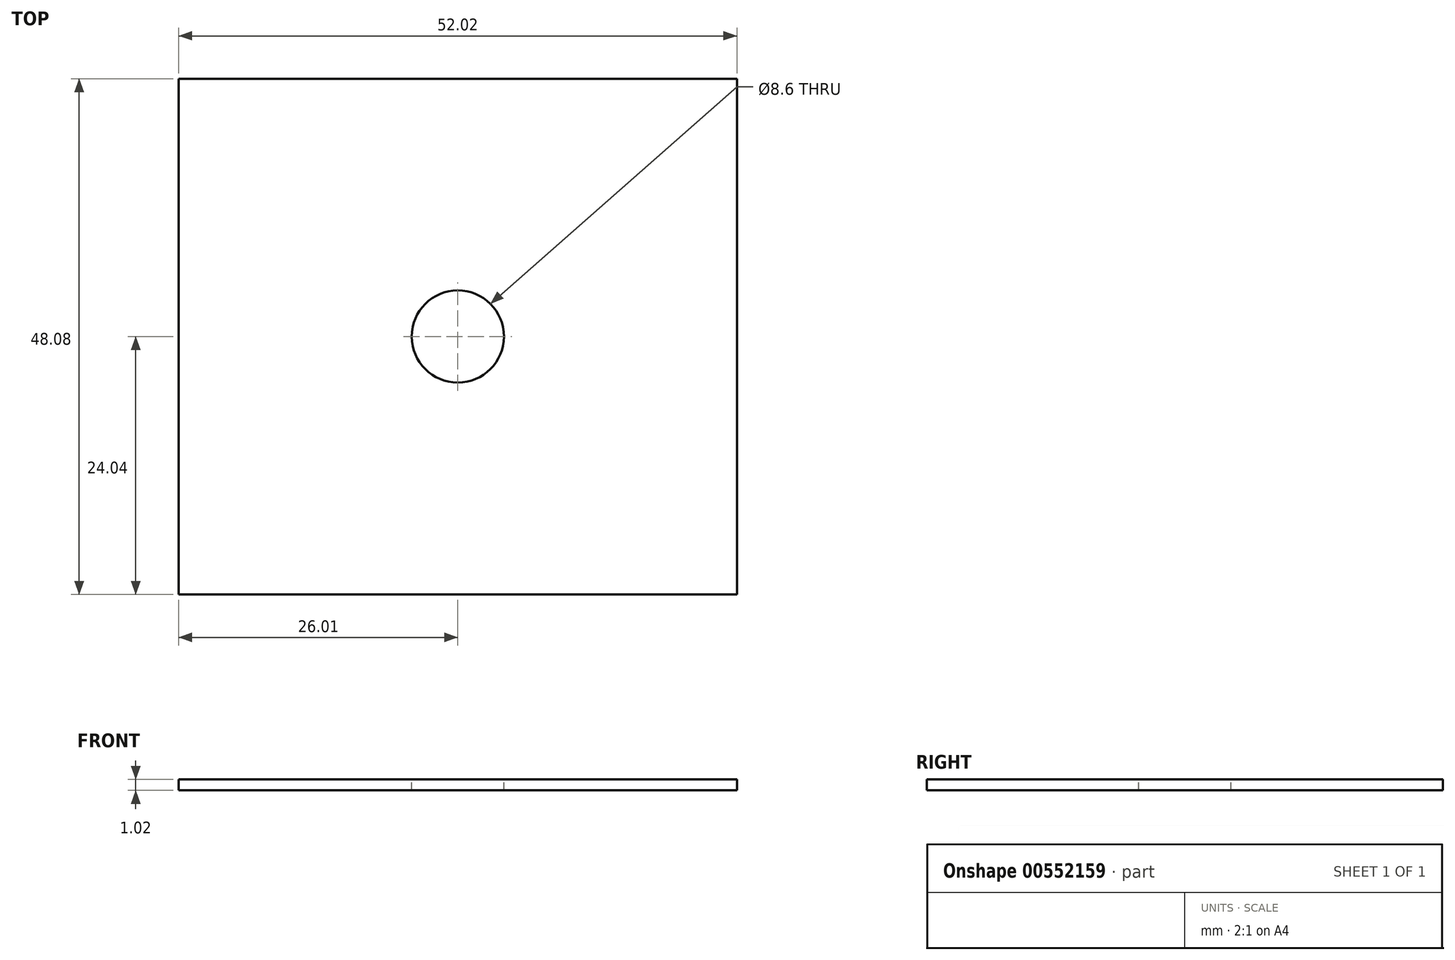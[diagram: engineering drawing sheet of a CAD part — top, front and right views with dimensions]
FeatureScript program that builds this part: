
annotation { "Feature Type Name" : "Feature", "Feature Type Description" : "" }
export const myFeature = defineFeature(function(context is Context, id is Id, definition is map)
    precondition{}
    {
        {
            var Q0;
            Q0=qCreatedBy(makeId("Top.planeOp"),FACE);
            var sketch = newSketch(context, id + "F0", { "sketchPlane" : qUnion([Q0])});
            skLineSegment(sketch, "E0.bottom", {"start": v(26.01, -24.04) * mm, "end": v(-26.01, -24.04) * mm});
            skLineSegment(sketch, "E0.top", {"start": v(26.01, 24.04) * mm, "end": v(-26.01, 24.04) * mm});
            skLineSegment(sketch, "E0.left", {"start": v(26.01, -24.04) * mm, "end": v(26.01, 24.04) * mm});
            skLineSegment(sketch, "E0.right", {"start": v(-26.01, -24.04) * mm, "end": v(-26.01, 24.04) * mm});
            skPoint(sketch, "E0.middle", {"position": v(0, 0) * mm});
            skSolve(sketch);
        }
        {
            var Q0;
            Q0 = qSketchRegion(id + "F0", true);
            extrude(context, id + "F1", {"entities" : qUnion([Q0]), "depth" : 1.02 * mm, "offsetDistance" : 25.4 * mm});
        }
        {
            var Q0;
            Q0=makeQuery(id+"F1.opExtrude","CAP_FACE",FACE,{"disambiguationData":[OSD([sQuery(id+"F0.wireOp",EDGE,"E0.bottom"),sQuery(id+"F0.wireOp",EDGE,"E0.top"),sQuery(id+"F0.wireOp",EDGE,"E0.left"),sQuery(id+"F0.wireOp",EDGE,"E0.right")])],"isStart":false});
            var sketch = newSketch(context, id + "F2", { "sketchPlane" : qUnion([Q0])});
            skCircle(sketch, "E1", {"center": v(0, 0) * mm, "radius": 4.3 * mm});
            skSolve(sketch);
        }
        {
            var Q0;
            Q0 = qSketchRegion(id + "F2", true);
            extrude(context, id + "F3", {"entities" : qUnion([Q0]), "operationType" : NewBodyOperationType.REMOVE, "oppositeDirection" : true, "depth" : 4.32 * mm, "offsetDistance" : 25.4 * mm});
        }
    });
